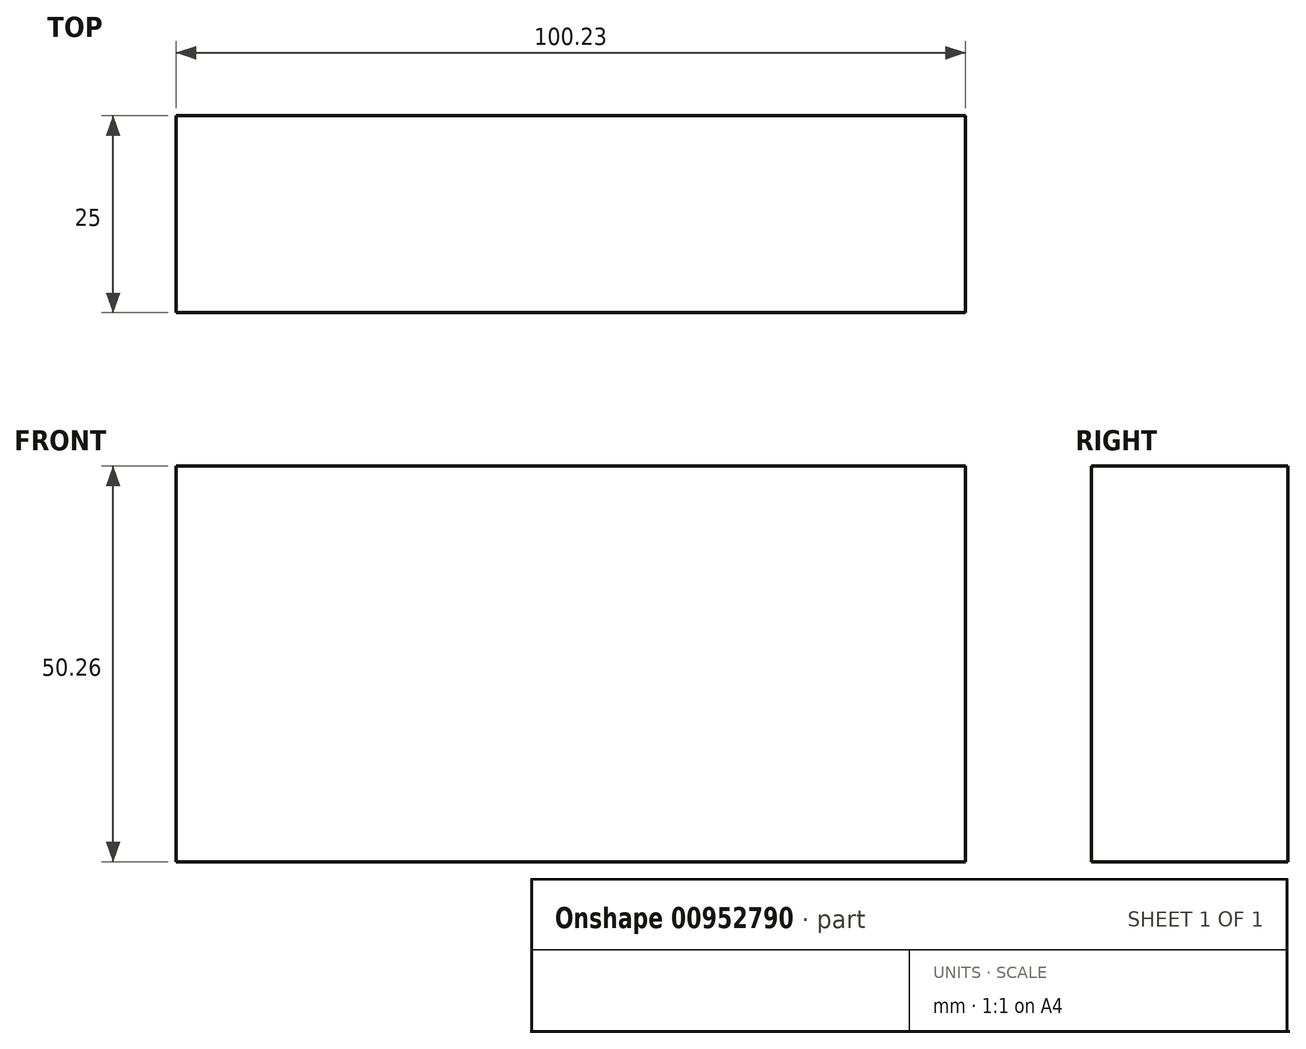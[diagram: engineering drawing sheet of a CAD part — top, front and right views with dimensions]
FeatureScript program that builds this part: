
annotation { "Feature Type Name" : "Feature", "Feature Type Description" : "" }
export const myFeature = defineFeature(function(context is Context, id is Id, definition is map)
    precondition{}
    {
        {
            var Q0;
            Q0=qCreatedBy(makeId("Front.planeOp"),FACE);
            var sketch = newSketch(context, id + "F0", { "sketchPlane" : qUnion([Q0])});
            skLineSegment(sketch, "E0.bottom", {"start": v(-35.21, 46.97) * mm, "end": v(65.02, 46.97) * mm});
            skLineSegment(sketch, "E0.top", {"start": v(-35.21, -3.3) * mm, "end": v(65.02, -3.3) * mm});
            skLineSegment(sketch, "E0.left", {"start": v(-35.21, 46.97) * mm, "end": v(-35.21, -3.3) * mm});
            skLineSegment(sketch, "E0.right", {"start": v(65.02, 46.97) * mm, "end": v(65.02, -3.3) * mm});
            skSolve(sketch);
        }
        {
            var Q0;
            Q0 = qSketchRegion(id + "F0", true);
            extrude(context, id + "F1", {"entities" : qUnion([Q0]), "depth" : 25 * mm, "offsetDistance" : 25 * mm});
        }
    });
